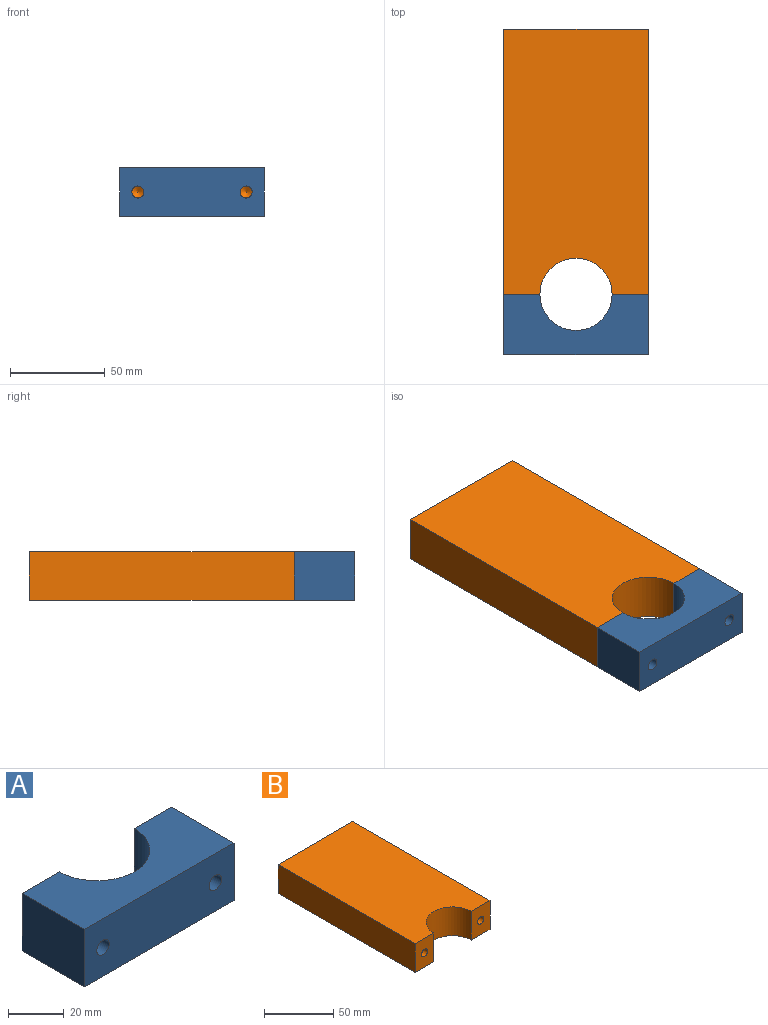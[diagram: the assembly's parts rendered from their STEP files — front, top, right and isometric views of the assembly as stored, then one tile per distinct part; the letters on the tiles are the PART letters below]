
ASSEMBLY  parts=2 mates=1
PART A: 10 faces, bbox 76.2x31.8x25.4 mm
  f0: plane 25.4x19.05mm, normal (0,1,0), area 452.2mm2, adj f1,f5,f6,f7,f9
  f1: plane 31.75x25.4mm, normal (-1,0,0), area 806.5mm2, adj f0,f2,f6,f7
  f2: plane 76.2x25.4mm, normal (0,-1,0), area 1872.1mm2, adj f1,f3,f6,f7,f8,f9
  f3: plane 31.75x25.4mm, normal (1,0,0), area 806.5mm2, adj f2,f4,f6,f7
  f4: plane 25.4x19.05mm, normal (0,1,0), area 452.2mm2, adj f3,f5,f6,f7,f8
  f5: cylinder r=19.05mm len=38.1mm, axis (0,0,-1), area 1520.1mm2, adj f0,f4,f6,f7
  f6: plane 76.2x31.75mm, normal (0,0,1), area 1849.3mm2, adj f0,f1,f2,f3,f4,f5
  f7: plane 76.2x31.75mm, normal (0,0,-1), area 1849.3mm2, adj f0,f1,f2,f3,f4,f5
  f8: cylinder r=3.17mm len=31.75mm, axis (0,1,0), area 633.4mm2, adj f2,f4
  f9: cylinder r=3.17mm len=31.75mm, axis (0,1,0), area 633.4mm2, adj f0,f2
PART B: 12 faces, bbox 76.2x139.7x25.4 mm
  f0: plane 139.7x25.4mm, normal (1,0,0), area 3548.4mm2, adj f1,f5,f6,f7
  f1: plane 76.2x25.4mm, normal (0,1,0), area 1935.5mm2, adj f0,f2,f6,f7
  f2: plane 139.7x25.4mm, normal (-1,0,0), area 3548.4mm2, adj f1,f3,f6,f7
  f3: plane 25.4x19.05mm, normal (0,-1,0), area 452.2mm2, adj f2,f4,f6,f7,f11
  f4: cylinder r=19.05mm len=38.1mm, axis (0,0,-1), area 1520.1mm2, adj f3,f5,f6,f7
  f5: plane 25.4x19.05mm, normal (0,-1,0), area 452.2mm2, adj f0,f4,f6,f7,f9
  f6: plane 139.7x76.2mm, normal (0,0,1), area 10075.1mm2, adj f0,f1,f2,f3,f4,f5
  f7: plane 139.7x76.2mm, normal (0,0,-1), area 10075.1mm2, adj f0,f1,f2,f3,f4,f5
  f8: cone r=0mm half-angle=59deg, axis (0,-1,0), area 36.9mm2, adj f9
  f9: cylinder r=3.17mm len=19.05mm, axis (0,-1,0), area 380mm2, adj f5,f8
  f10: cone r=0mm half-angle=59deg, axis (0,-1,0), area 36.9mm2, adj f11
  f11: cylinder r=3.17mm len=19.05mm, axis (0,-1,0), area 380mm2, adj f3,f10
PLACE A t=(2.71,-122.15,-58.15)mm
PLACE B t=(2.71,17.55,-58.15)mm
MATE parallel A.f8 <-> B.f8  axis (0,1,0) through (69.39,-122.15,-45.45)mm
